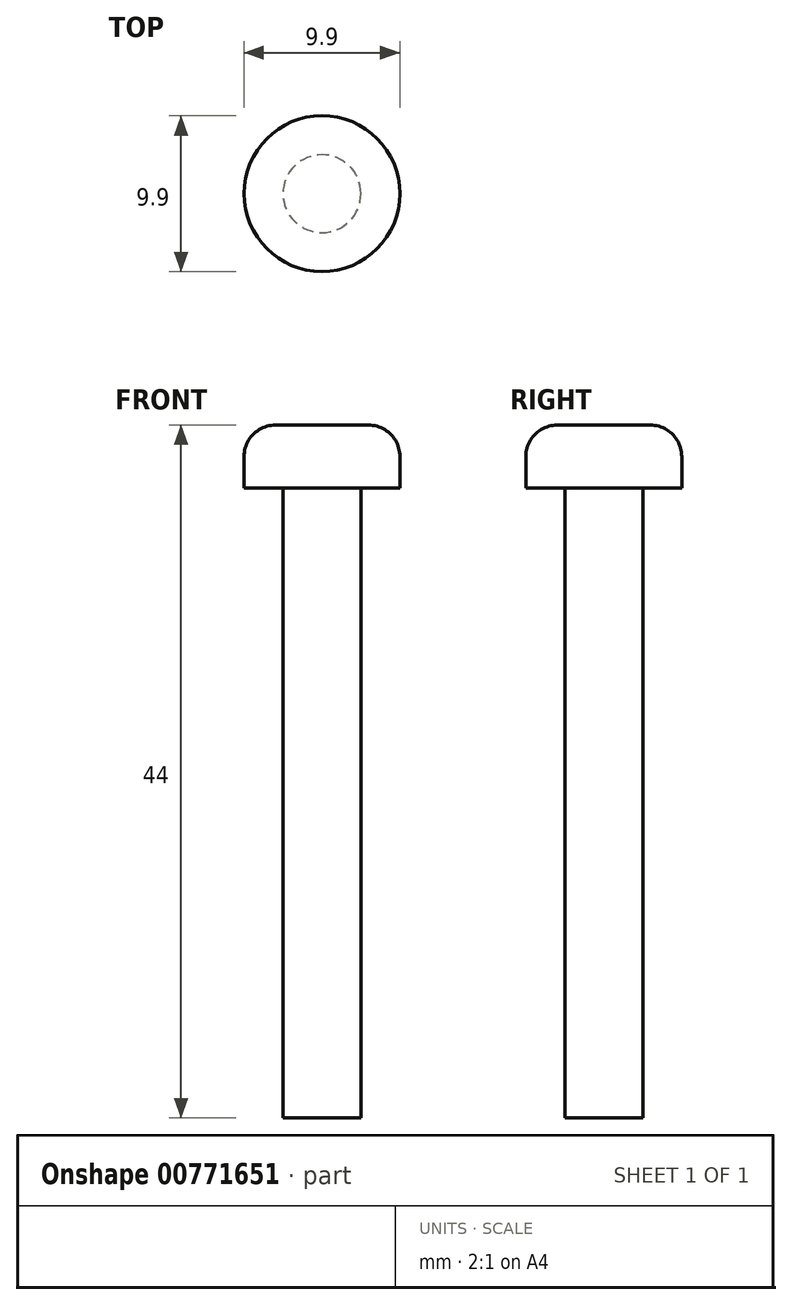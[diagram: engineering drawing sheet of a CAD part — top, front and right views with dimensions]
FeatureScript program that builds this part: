
annotation { "Feature Type Name" : "Feature", "Feature Type Description" : "" }
export const myFeature = defineFeature(function(context is Context, id is Id, definition is map)
    precondition{}
    {
        {
            var Q0;
            Q0=qCreatedBy(makeId("Top.planeOp"),FACE);
            var sketch = newSketch(context, id + "F0", { "sketchPlane" : qUnion([Q0])});
            skCircle(sketch, "E0", {"center": v(0, 0) * mm, "radius": 4.95 * mm});
            skSolve(sketch);
        }
        {
            var Q0;
            Q0 = qSketchRegion(id + "F0", true);
            extrude(context, id + "F1", {"entities" : qUnion([Q0]), "depth" : 4 * mm, "offsetDistance" : 25 * mm});
        }
        {
            var Q0;
            Q0=makeQuery(id+"F1.opExtrude","CAP_EDGE",EDGE,{"disambiguationData":[OSD([sQuery(id+"F0.wireOp",EDGE,"E0")])],"isStart":false});
            fillet(context, id + "F2", {"entities" : qUnion([Q0]), "radius" : 2 * mm, "tangentPropagation" : true, "allowEdgeOverflow" : false});
        }
        {
            var Q0;
            Q0=makeQuery(id+"F1.opExtrude","CAP_FACE",FACE,{"disambiguationData":[OSD([sQuery(id+"F0.wireOp",EDGE,"E0")])],"isStart":true});
            var sketch = newSketch(context, id + "F3", { "sketchPlane" : qUnion([Q0])});
            skCircle(sketch, "E1", {"center": v(0, 0) * mm, "radius": 2.48 * mm});
            skSolve(sketch);
        }
        {
            var Q0;
            Q0 = qSketchRegion(id + "F3", true);
            extrude(context, id + "F4", {"entities" : qUnion([Q0]), "operationType" : NewBodyOperationType.ADD, "depth" : 25 * mm, "offsetDistance" : 25 * mm});
        }
        {
            var Q0;
            Q0 = qSketchRegion(id + "F3", true);
            extrude(context, id + "F5", {"entities" : qUnion([Q0]), "operationType" : NewBodyOperationType.ADD, "depth" : 40 * mm, "offsetDistance" : 25 * mm});
        }
    });
